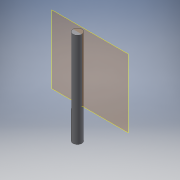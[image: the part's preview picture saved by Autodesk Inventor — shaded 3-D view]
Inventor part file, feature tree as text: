
AUTODESK INVENTOR PART (.ipt)
format: ipt  version: 2019 (Build 230136000, 136)  size: 101,888 bytes
history: native  units: in
note: dims shown in document units (in); Inventor stores cm internally (conversion verified against a paired STEP export)
features: sketch x2, other x2, plane x1, revolve x1, extrude x1
ambient origin geometry x8: Origin, YZ Plane, XZ Plane, XY Plane, X Axis, Y Axis, Z Axis, Center Point
bodies: Solid1 (feature_tree)
feature tree (7):
  plane  "Work Plane1"
  revolve  "Revolution1"  [1 undecoded]
  extrude  "Extrusion1"  Depth=0.3661in
  sketch  "Sketch1"  dims[d0=1.2598in d1=0.1181in]
  sketch  "Sketch2"  dims[d2=90.0deg d3=0.0394in d4=0.3661in d5=0.0in]
  other  "Assembly1"
  other  "Motor-Body:1"
note: 1 required parameter value undecoded (feature->parameter linkage not recoverable at this tier; creation-order binding heuristic only, values carry confidence <= 0.55)
